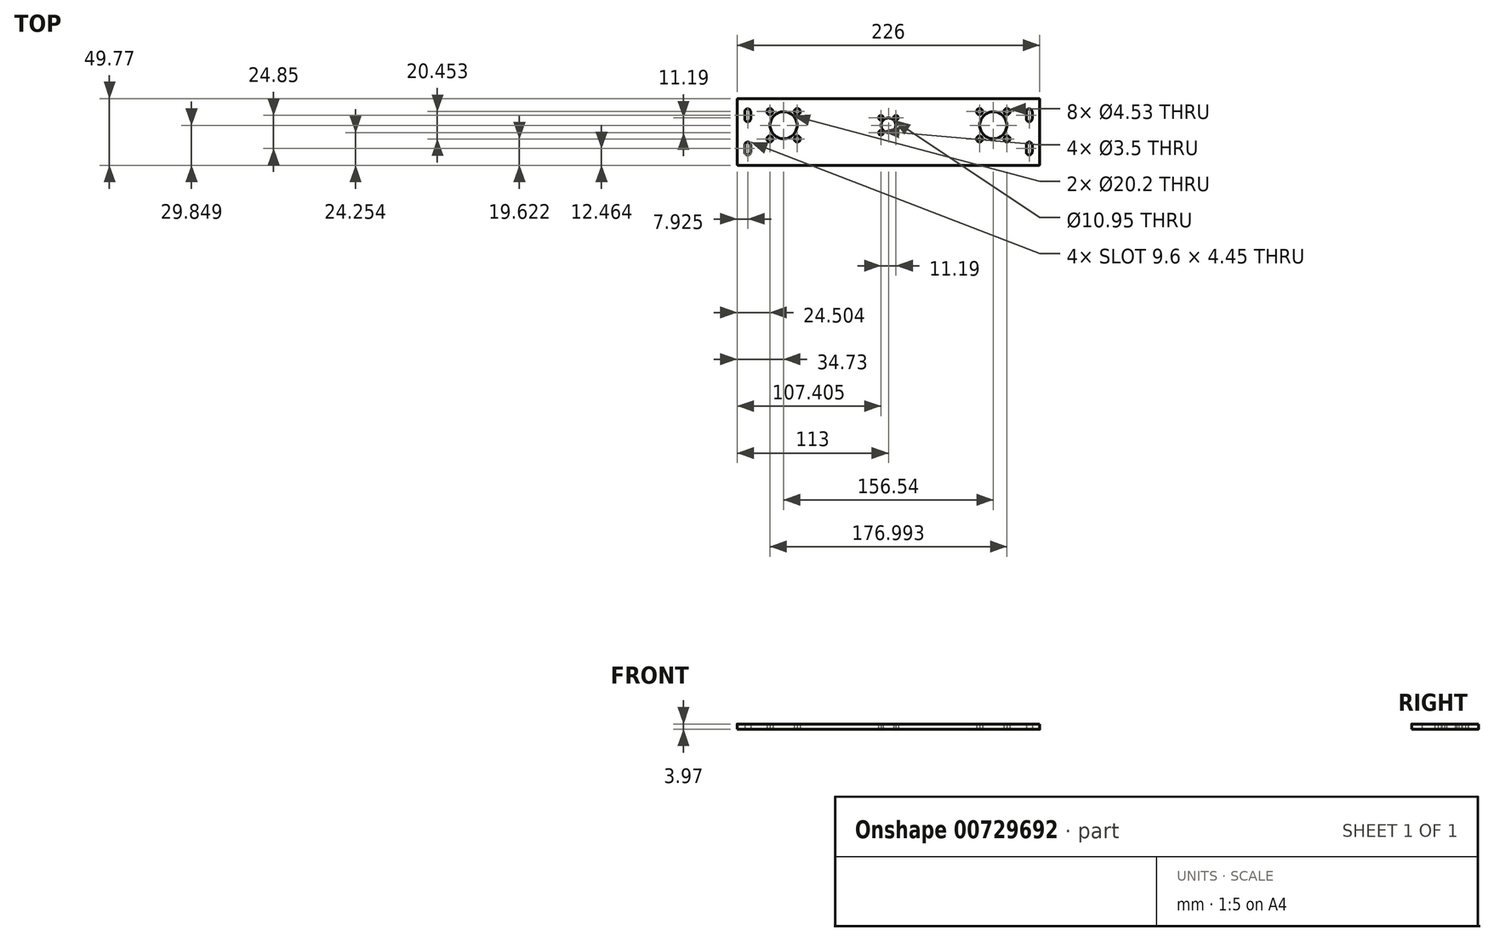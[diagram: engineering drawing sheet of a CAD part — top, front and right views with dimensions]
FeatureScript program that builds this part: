
annotation { "Feature Type Name" : "Feature", "Feature Type Description" : "" }
export const myFeature = defineFeature(function(context is Context, id is Id, definition is map)
    precondition{}
    {
        {
            var Q0;
            Q0=qCreatedBy(makeId("Top.planeOp"),FACE);
            var sketch = newSketch(context, id + "F0", { "sketchPlane" : qUnion([Q0])});
            skLineSegment(sketch, "E0.bottom", {"start": v(-111.45, 1.5) * mm, "end": v(113.55, 1.5) * mm});
            skLineSegment(sketch, "E0.top", {"start": v(-111.45, -48.27) * mm, "end": v(113.55, -48.27) * mm});
            skLineSegment(sketch, "E0.left", {"start": v(-111.95, 1) * mm, "end": v(-111.95, -47.77) * mm});
            skLineSegment(sketch, "E0.right", {"start": v(114.05, 1) * mm, "end": v(114.05, -47.77) * mm});
            skLineSegment(sketch, "E1", {"start": v(1.05, 1.5) * mm, "end": v(1.05, -48.27) * mm, "construction": true});
            skCircle(sketch, "E2", {"center": v(1.05, -18.42) * mm, "radius": 5.47 * mm});
            skLineSegment(sketch, "E3", {"start": v(-111.95, -18.42) * mm, "end": v(114.05, -18.42) * mm, "construction": true});
            skPoint(sketch, "E3.endSnap0", {"position": v(114.05, -23.38) * mm});
            skCircle(sketch, "E4", {"center": v(79.32, -18.42) * mm, "radius": 10.1 * mm});
            skLineSegment(sketch, "E5", {"start": v(106.13, 1.5) * mm, "end": v(106.13, -48.27) * mm, "construction": true});
            skArc(sketch, "E6", {"start": v(108.35, -8.38) * mm, "mid": v(106.13, -6.16) * mm, "end": v(103.9, -8.38) * mm});
            skArc(sketch, "E7", {"start": v(103.9, -13.53) * mm, "mid": v(106.13, -15.76) * mm, "end": v(108.35, -13.53) * mm});
            skLineSegment(sketch, "E8", {"start": v(114.05, -23.38) * mm, "end": v(-111.95, -23.38) * mm, "construction": true});
            skLineSegment(sketch, "E9", {"start": v(103.9, -8.38) * mm, "end": v(108.35, -8.38) * mm, "construction": true});
            skLineSegment(sketch, "E10", {"start": v(103.9, -13.53) * mm, "end": v(108.35, -13.53) * mm, "construction": true});
            skLineSegment(sketch, "E11", {"start": v(103.9, -8.38) * mm, "end": v(103.9, -13.53) * mm});
            skLineSegment(sketch, "E12", {"start": v(108.35, -8.38) * mm, "end": v(108.35, -13.53) * mm});
            skArc(sketch, "E13.MirrorCS", {"start": v(103.9, -33.23) * mm, "mid": v(106.13, -31) * mm, "end": v(108.35, -33.23) * mm});
            skLineSegment(sketch, "E14.MirrorCS", {"start": v(103.9, -38.38) * mm, "end": v(103.9, -33.23) * mm});
            skLineSegment(sketch, "E15.MirrorCS", {"start": v(108.35, -38.38) * mm, "end": v(108.35, -33.23) * mm});
            skArc(sketch, "E16.MirrorCS", {"start": v(108.35, -38.38) * mm, "mid": v(106.13, -40.6) * mm, "end": v(103.9, -38.38) * mm});
            skLineSegment(sketch, "E17.MirrorCS", {"start": v(-101.8, -38.38) * mm, "end": v(-101.8, -33.23) * mm});
            skArc(sketch, "E18.MirrorCS", {"start": v(-106.25, -38.38) * mm, "mid": v(-104.02, -40.6) * mm, "end": v(-101.8, -38.38) * mm});
            skLineSegment(sketch, "E19.MirrorCS", {"start": v(-106.25, -38.38) * mm, "end": v(-106.25, -33.23) * mm});
            skArc(sketch, "E20.MirrorCS", {"start": v(-101.8, -33.23) * mm, "mid": v(-104.02, -31) * mm, "end": v(-106.25, -33.23) * mm});
            skLineSegment(sketch, "E21.MirrorCS", {"start": v(-101.8, -13.53) * mm, "end": v(-106.25, -13.53) * mm, "construction": true});
            skLineSegment(sketch, "E22.MirrorCS", {"start": v(-104.02, 1.5) * mm, "end": v(-104.02, -48.27) * mm, "construction": true});
            skLineSegment(sketch, "E23.MirrorCS", {"start": v(-101.8, -8.38) * mm, "end": v(-106.25, -8.38) * mm, "construction": true});
            skLineSegment(sketch, "E24.MirrorCS", {"start": v(-106.25, -8.38) * mm, "end": v(-106.25, -13.53) * mm});
            skArc(sketch, "E25.MirrorCS", {"start": v(-106.25, -8.38) * mm, "mid": v(-104.02, -6.16) * mm, "end": v(-101.8, -8.38) * mm});
            skLineSegment(sketch, "E26.MirrorCS", {"start": v(-101.8, -8.38) * mm, "end": v(-101.8, -13.53) * mm});
            skArc(sketch, "E27.MirrorCS", {"start": v(-101.8, -13.53) * mm, "mid": v(-104.02, -15.76) * mm, "end": v(-106.25, -13.53) * mm});
            skLineSegment(sketch, "E28", {"start": v(79.32, -18.42) * mm, "end": v(89.55, -28.65) * mm, "construction": true});
            skCircle(sketch, "E29", {"center": v(89.55, -28.65) * mm, "radius": 2.27 * mm});
            skCircle(sketch, "E30.1.0", {"center": v(89.55, -8.2) * mm, "radius": 2.27 * mm});
            skCircle(sketch, "E30.2.0", {"center": v(69.1, -8.2) * mm, "radius": 2.27 * mm});
            skCircle(sketch, "E30.3.0", {"center": v(69.1, -28.65) * mm, "radius": 2.27 * mm});
            skCircle(sketch, "E31.MirrorC", {"center": v(-77.22, -18.42) * mm, "radius": 10.1 * mm});
            skCircle(sketch, "E32.MirrorC", {"center": v(-87.45, -28.65) * mm, "radius": 2.27 * mm});
            skCircle(sketch, "E33.MirrorC", {"center": v(-67, -28.65) * mm, "radius": 2.27 * mm});
            skCircle(sketch, "E34.MirrorC", {"center": v(-67, -8.2) * mm, "radius": 2.27 * mm});
            skCircle(sketch, "E35.MirrorC", {"center": v(-87.45, -8.2) * mm, "radius": 2.27 * mm});
            skLineSegment(sketch, "E36", {"start": v(1.05, -18.42) * mm, "end": v(6.53, -18.42) * mm, "construction": true});
            skLineSegment(sketch, "E37", {"start": v(1.05, -18.42) * mm, "end": v(6.65, -24.02) * mm, "construction": true});
            skCircle(sketch, "E38", {"center": v(6.65, -24.02) * mm, "radius": 1.75 * mm});
            skCircle(sketch, "E39.1.0", {"center": v(6.65, -12.83) * mm, "radius": 1.75 * mm});
            skCircle(sketch, "E39.2.0", {"center": v(-4.54, -12.83) * mm, "radius": 1.75 * mm});
            skCircle(sketch, "E39.3.0", {"center": v(-4.54, -24.02) * mm, "radius": 1.75 * mm});
            skPoint(sketch, "E40.visualSharp", {"position": v(-111.95, 1.5) * mm});
            skArc(sketch, "E40.filletArc", {"start": v(-111.45, 1.5) * mm, "mid": v(-111.8, 1.36) * mm, "end": v(-111.95, 1) * mm});
            skPoint(sketch, "E41.visualSharp", {"position": v(-111.95, -48.27) * mm});
            skArc(sketch, "E41.filletArc", {"start": v(-111.95, -47.77) * mm, "mid": v(-111.8, -48.12) * mm, "end": v(-111.45, -48.27) * mm});
            skPoint(sketch, "E42.visualSharp", {"position": v(114.05, 1.5) * mm});
            skArc(sketch, "E42.filletArc", {"start": v(114.05, 1) * mm, "mid": v(113.9, 1.36) * mm, "end": v(113.55, 1.5) * mm});
            skPoint(sketch, "E43.visualSharp", {"position": v(114.05, -48.27) * mm});
            skArc(sketch, "E43.filletArc", {"start": v(113.55, -48.27) * mm, "mid": v(113.9, -48.12) * mm, "end": v(114.05, -47.77) * mm});
            skSolve(sketch);
        }
        {
            var Q0;
            Q0=makeQuery(id+"F0.imprint","IMPRINT",FACE,{"disambiguationData":[TD([[makeQuery(id+"F0.imprint","IMPRINT",EDGE,{"derivedFrom":sQuery(id+"F0.wireOp",EDGE,"E0.bottom")}),-1.0]])]});
            extrude(context, id + "F1", {"entities" : qUnion([Q0]), "depth" : 3.97 * mm, "offsetDistance" : 25 * mm});
        }
    });
